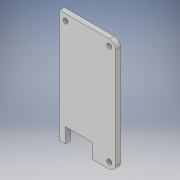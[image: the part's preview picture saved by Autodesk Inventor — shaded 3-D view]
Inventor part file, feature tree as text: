
AUTODESK INVENTOR PART (.ipt)
format: ipt  version: 2019 (Build 230136000, 136)  size: 121,344 bytes
history: native  units: in
note: dims shown in document units (in); Inventor stores cm internally (conversion verified against a paired STEP export)
features: sketch x2, extrude x1, hole x1
ambient origin geometry x8: Origin, YZ Plane, XZ Plane, XY Plane, X Axis, Y Axis, Z Axis, Center Point
bodies: Solid1 (feature_tree)
feature tree (4):
  extrude  "Scanner Cover"  Depth=0.3in
  hole  "Screw Holes"  [1 undecoded]
  sketch  "Sketch1"  dims[d1=2.27in d3=0.3in]
  sketch  "Sketch2"  dims[d5=0.1in d6=0.0in d7=0.125in d8=0.125in d9=0.125in d10=0.125in d11=0.47in d12=1.13in d13=0.125in d14=0.1in d15=0.75in d16=0.375in d17=0.25in d18=0.5635in d19=1.0in d20=0.8108in d21=0.3in d22=0.125in d23=0.125in]
note: 1 required parameter value undecoded (feature->parameter linkage not recoverable at this tier; creation-order binding heuristic only, values carry confidence <= 0.55)
